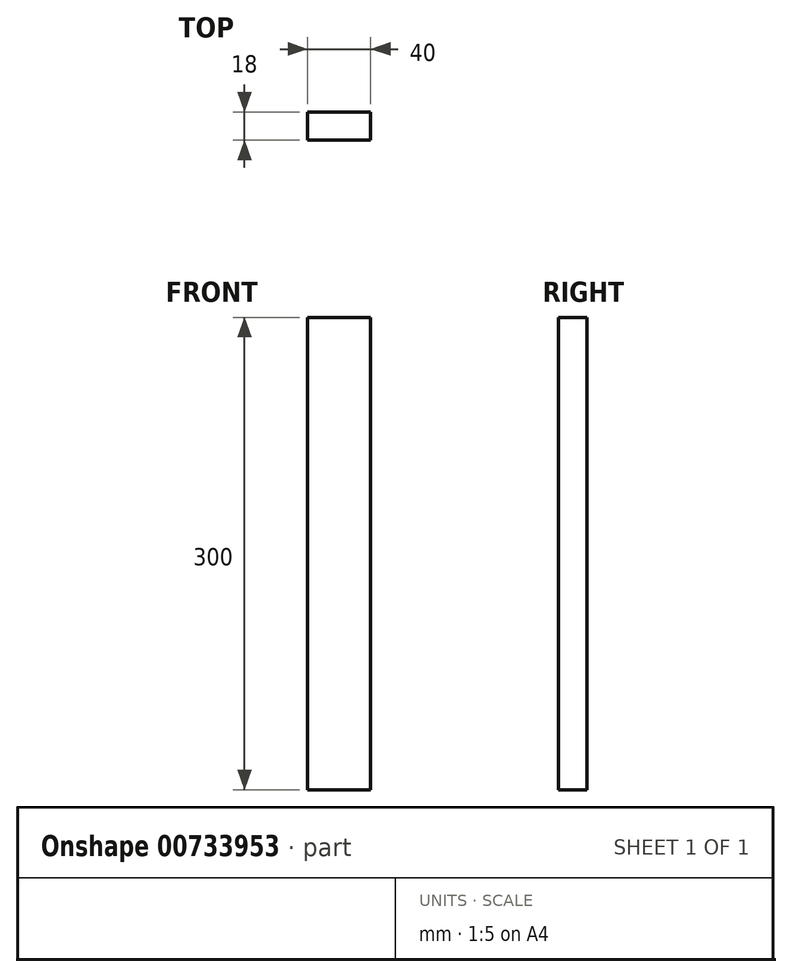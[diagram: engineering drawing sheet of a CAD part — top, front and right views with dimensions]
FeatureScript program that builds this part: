
annotation { "Feature Type Name" : "Feature", "Feature Type Description" : "" }
export const myFeature = defineFeature(function(context is Context, id is Id, definition is map)
    precondition{}
    {
        {
            var Q0;
            Q0=qCreatedBy(makeId("Front.planeOp"),FACE);
            var sketch = newSketch(context, id + "F0", { "sketchPlane" : qUnion([Q0])});
            skLineSegment(sketch, "E0.bottom", {"start": v(0, 0) * mm, "end": v(40, 0) * mm});
            skLineSegment(sketch, "E0.top", {"start": v(0, 300) * mm, "end": v(40, 300) * mm});
            skLineSegment(sketch, "E0.left", {"start": v(0, 0) * mm, "end": v(0, 300) * mm});
            skLineSegment(sketch, "E0.right", {"start": v(40, 0) * mm, "end": v(40, 300) * mm});
            skSolve(sketch);
        }
        {
            var Q0;
            Q0 = qSketchRegion(id + "F0", true);
            extrude(context, id + "F1", {"entities" : qUnion([Q0]), "oppositeDirection" : true, "depth" : 18 * mm, "offsetDistance" : 25 * mm});
        }
    });
